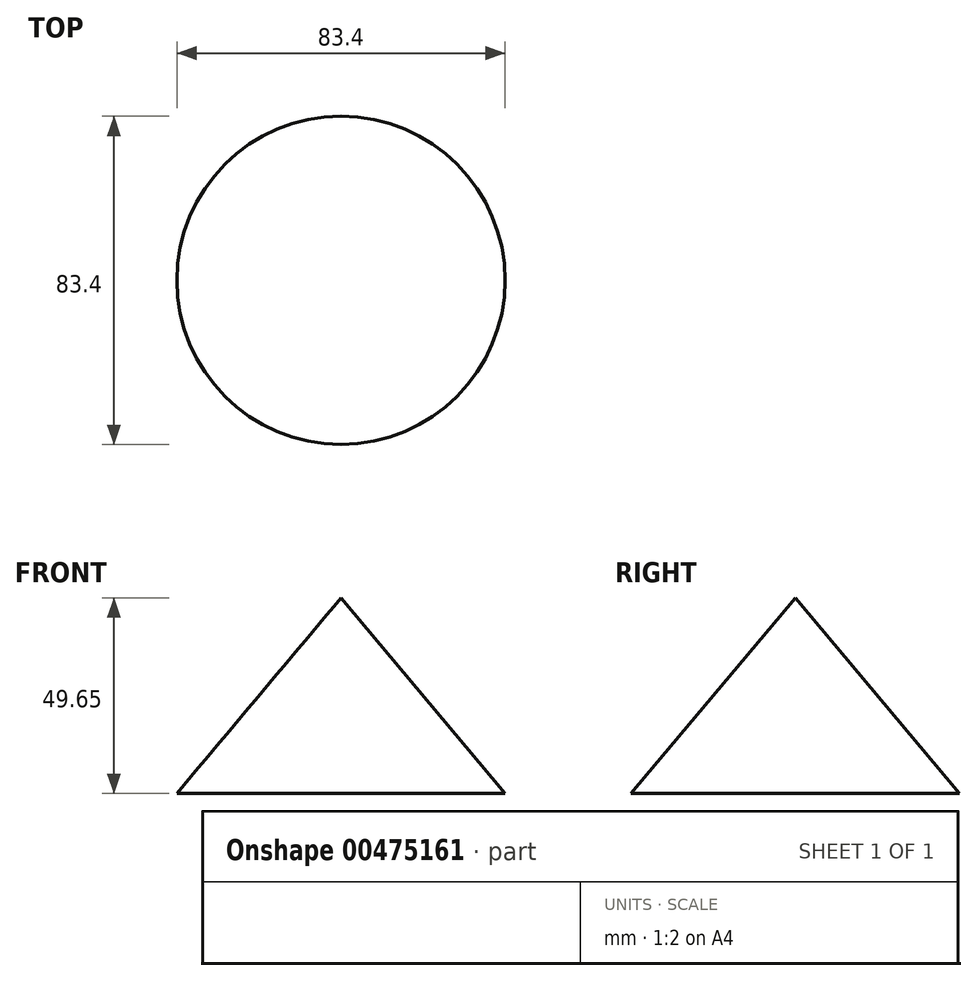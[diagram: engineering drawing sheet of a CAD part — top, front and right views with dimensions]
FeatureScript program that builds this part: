
annotation { "Feature Type Name" : "Feature", "Feature Type Description" : "" }
export const myFeature = defineFeature(function(context is Context, id is Id, definition is map)
    precondition{}
    {
        {
            var Q0;
            Q0=qCreatedBy(makeId("Front.planeOp"),FACE);
            var sketch = newSketch(context, id + "F0", { "sketchPlane" : qUnion([Q0])});
            skLineSegment(sketch, "E0", {"start": v(0, 0) * mm, "end": v(41.7, 0) * mm});
            skLineSegment(sketch, "E1", {"start": v(41.7, 0) * mm, "end": v(0, 49.65) * mm});
            skLineSegment(sketch, "E2", {"start": v(0, 49.65) * mm, "end": v(0, 0) * mm});
            skSolve(sketch);
        }
        {
            var Q0;
            Q0=makeQuery(id+"F0.imprint","IMPRINT",FACE,{"disambiguationData":[TD([[makeQuery(id+"F0.imprint","IMPRINT",EDGE,{"derivedFrom":sQuery(id+"F0.wireOp",EDGE,"E0")}),1.0]])]});
            var Q1;
            Q1=sQuery(id+"F0.wireOp",EDGE,"E2");
            revolve(context, id + "F1", {"entities" : qUnion([Q0]), "axis" : qUnion([Q1]), "revolveType" : RevolveType.FULL});
        }
    });
